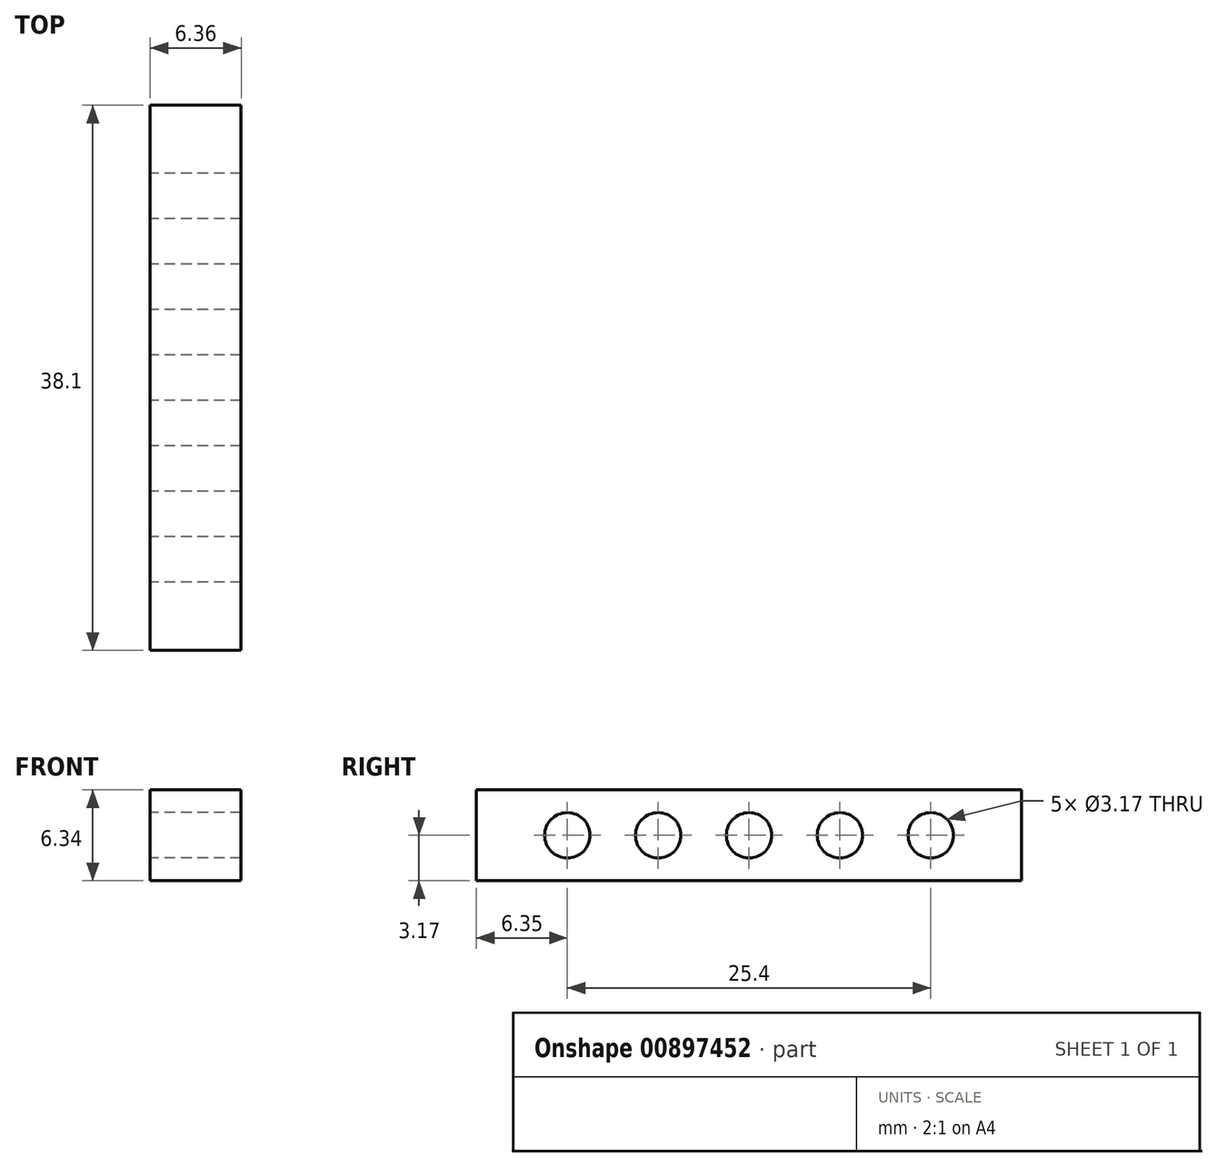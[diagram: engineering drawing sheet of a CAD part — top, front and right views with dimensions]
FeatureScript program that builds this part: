
annotation { "Feature Type Name" : "Feature", "Feature Type Description" : "" }
export const myFeature = defineFeature(function(context is Context, id is Id, definition is map)
    precondition{}
    {
        {
            var Q0;
            Q0=qCreatedBy(makeId("Right.planeOp"),FACE);
            var sketch = newSketch(context, id + "F0", { "sketchPlane" : qUnion([Q0])});
            skLineSegment(sketch, "E0.bottom", {"start": v(-19.05, 3.17) * mm, "end": v(19.05, 3.18) * mm});
            skLineSegment(sketch, "E0.top", {"start": v(-19.05, -3.18) * mm, "end": v(19.05, -3.17) * mm});
            skLineSegment(sketch, "E0.left", {"start": v(-19.05, 3.17) * mm, "end": v(-19.05, -3.18) * mm});
            skLineSegment(sketch, "E0.right", {"start": v(19.05, 3.18) * mm, "end": v(19.05, -3.17) * mm});
            skCircle(sketch, "E1", {"center": v(-12.7, 0) * mm, "radius": 1.59 * mm});
            skLineSegment(sketch, "E2", {"start": v(-9.52, 3.18) * mm, "end": v(-9.52, -3.18) * mm, "construction": true});
            skLineSegment(sketch, "E3", {"start": v(-15.88, -3.18) * mm, "end": v(-15.88, 3.18) * mm, "construction": true});
            skCircle(sketch, "E4.MirrorC", {"center": v(-6.35, 0) * mm, "radius": 1.59 * mm});
            skLineSegment(sketch, "E5.MirrorCS", {"start": v(-3.17, -3.17) * mm, "end": v(-3.17, 3.18) * mm, "construction": true});
            skCircle(sketch, "E6.MirrorC", {"center": v(0, 0) * mm, "radius": 1.59 * mm});
            skLineSegment(sketch, "E7.MirrorCS", {"start": v(3.18, 3.17) * mm, "end": v(3.18, -3.18) * mm, "construction": true});
            skCircle(sketch, "E8.MirrorC", {"center": v(6.35, 0) * mm, "radius": 1.59 * mm});
            skLineSegment(sketch, "E9.MirrorCS", {"start": v(9.53, -3.18) * mm, "end": v(9.53, 3.17) * mm, "construction": true});
            skCircle(sketch, "E10.MirrorC", {"center": v(12.7, 0) * mm, "radius": 1.59 * mm});
            skLineSegment(sketch, "E11.MirrorCS", {"start": v(15.88, 3.17) * mm, "end": v(15.88, -3.18) * mm, "construction": true});
            skSolve(sketch);
        }
        {
            var Q0;
            Q0=makeQuery(id+"F0.imprint","IMPRINT",FACE,{"disambiguationData":[TD([[makeQuery(id+"F0.imprint","IMPRINT",EDGE,{"derivedFrom":sQuery(id+"F0.wireOp",EDGE,"E0.bottom")}),-1.0]])]});
            extrude(context, id + "F1", {"entities" : qUnion([Q0]), "depth" : 3.17 * mm, "offsetDistance" : 25.4 * mm, "hasSecondDirection" : true, "secondDirectionOppositeDirection" : true, "secondDirectionDepth" : 3.17 * mm});
        }
    });
